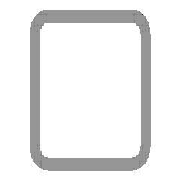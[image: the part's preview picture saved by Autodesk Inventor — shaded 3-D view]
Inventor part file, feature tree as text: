
AUTODESK INVENTOR PART (.ipt)
format: ipt  version: 2022 (Build 260153000, 153)  size: 655,872 bytes
history: native  units: mm (DEFAULTED — no unit token found)
features: other x8, sketch x3, plane x2, surface_op x2, split x1
ambient origin geometry x8: Origin, YZ Plane, XZ Plane, XY Plane, X Axis, Y Axis, Z Axis, Center Point
bodies: Solid1 (feature_tree), Body (feature_tree), Solid7 (feature_tree), Solid8 (feature_tree)
feature tree (16):
  parser-record x1  (decoder bookkeeping rows leaked as tree rows — omitted from the tree; the rows remain in map.json)
  other  "Driven Length"
  other  "Start Plane"
  other  "End Plane"
  plane  "Work Plane4"
  split  "Split1"
  sketch  "Sketch"  dims[d7=4.0mm d9=40.0mm d11=40.0mm d12=2.0mm d13=-0.0mm d14=310.0mm d15=20.0mm d16=20.0mm d17=90.0deg d18=310.0mm d55=5.0mm d56=5.0mm d57=5.0mm d58=5.0mm d59=5.0mm d60=5.0mm d61=5.0mm d62=5.0mm d63=0.0mm d64=5.0mm d65=5.0mm d66=5.0mm d67=5.0mm d68=5.0mm d69=5.0mm d70=5.0mm d71=5.0mm d72=0.0mm]
  sketch  "Sketch3"  dims[d3=310.0mm]
  plane  "Work Plane3"
  sketch  "Sketch4"  dims[d4=0.0mm]
  other  "Srf12"
  other  "Srf13"
  other  "Srf10"
  other  "Srf11"
  surface_op  "Boundary Patch5"
  surface_op  "Boundary Patch6"
